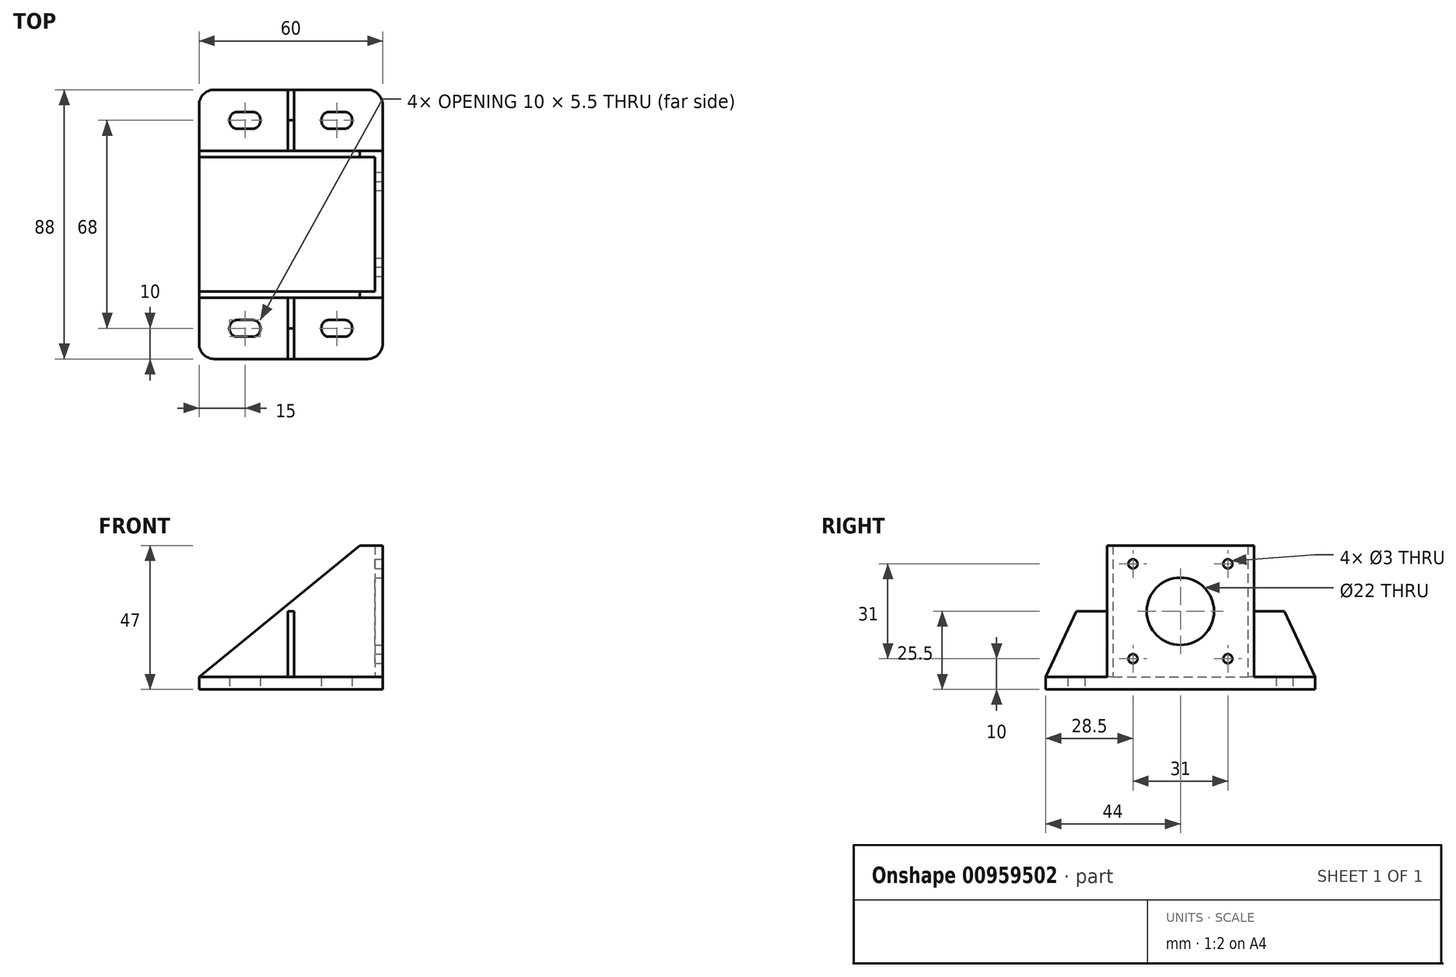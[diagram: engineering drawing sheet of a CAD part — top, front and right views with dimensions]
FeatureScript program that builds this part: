
annotation { "Feature Type Name" : "Feature", "Feature Type Description" : "" }
export const myFeature = defineFeature(function(context is Context, id is Id, definition is map)
    precondition{}
    {
        {
            var Q0;
            Q0=qCreatedBy(makeId("Top.planeOp"),FACE);
            var sketch = newSketch(context, id + "F0", { "sketchPlane" : qUnion([Q0])});
            skLineSegment(sketch, "E0.bottom", {"start": v(30, -24) * mm, "end": v(-30, -24) * mm});
            skLineSegment(sketch, "E0.top", {"start": v(30, 24) * mm, "end": v(-30, 24) * mm});
            skLineSegment(sketch, "E0.left", {"start": v(30, -24) * mm, "end": v(30, 24) * mm});
            skLineSegment(sketch, "E0.right", {"start": v(-30, -24) * mm, "end": v(-30, 24) * mm});
            skPoint(sketch, "E0.middle", {"position": v(0, 0) * mm});
            skLineSegment(sketch, "E1", {"start": v(-30, 22) * mm, "end": v(27.5, 22) * mm});
            skLineSegment(sketch, "E2", {"start": v(27.5, 22) * mm, "end": v(27.5, -22) * mm});
            skLineSegment(sketch, "E3", {"start": v(27.5, -22) * mm, "end": v(-30, -22) * mm});
            skLineSegment(sketch, "E4", {"start": v(30, -24) * mm, "end": v(30, -44) * mm});
            skLineSegment(sketch, "E5", {"start": v(30, -44) * mm, "end": v(-30, -44) * mm});
            skLineSegment(sketch, "E6", {"start": v(-30, -44) * mm, "end": v(-30, -24) * mm});
            skLineSegment(sketch, "E7", {"start": v(30, 24) * mm, "end": v(30, 44) * mm});
            skLineSegment(sketch, "E8", {"start": v(30, 44) * mm, "end": v(-30, 44) * mm});
            skLineSegment(sketch, "E9", {"start": v(-30, 44) * mm, "end": v(-30, 24) * mm});
            skLineSegment(sketch, "E10", {"start": v(-1, -44) * mm, "end": v(-1, -24) * mm});
            skLineSegment(sketch, "E11", {"start": v(1, -24) * mm, "end": v(1, -44) * mm});
            skLineSegment(sketch, "E12.MirrorCS", {"start": v(-1, 44) * mm, "end": v(-1, 24) * mm});
            skLineSegment(sketch, "E13.MirrorCS", {"start": v(1, 24) * mm, "end": v(1, 44) * mm});
            skLineSegment(sketch, "E14", {"start": v(30, -34) * mm, "end": v(-30, -34) * mm, "construction": true});
            skLineSegment(sketch, "E15.bottom", {"start": v(20, -36.75) * mm, "end": v(10, -36.75) * mm});
            skLineSegment(sketch, "E15.top", {"start": v(20, -31.25) * mm, "end": v(10, -31.25) * mm});
            skLineSegment(sketch, "E15.left", {"start": v(20, -36.75) * mm, "end": v(20, -31.25) * mm});
            skLineSegment(sketch, "E15.right", {"start": v(10, -36.75) * mm, "end": v(10, -31.25) * mm});
            skPoint(sketch, "E15.middle", {"position": v(15, -34) * mm});
            skLineSegment(sketch, "E16.bottom", {"start": v(-10, -36.75) * mm, "end": v(-20, -36.75) * mm});
            skLineSegment(sketch, "E16.top", {"start": v(-10, -31.25) * mm, "end": v(-20, -31.25) * mm});
            skLineSegment(sketch, "E16.left", {"start": v(-10, -36.75) * mm, "end": v(-10, -31.25) * mm});
            skLineSegment(sketch, "E16.right", {"start": v(-20, -36.75) * mm, "end": v(-20, -31.25) * mm});
            skPoint(sketch, "E16.middle", {"position": v(-15, -34) * mm});
            skLineSegment(sketch, "E17.MirrorCS", {"start": v(20, 31.25) * mm, "end": v(10, 31.25) * mm});
            skLineSegment(sketch, "E18.MirrorCS", {"start": v(20, 36.75) * mm, "end": v(20, 31.25) * mm});
            skLineSegment(sketch, "E19.MirrorCS", {"start": v(20, 36.75) * mm, "end": v(10, 36.75) * mm});
            skLineSegment(sketch, "E20.MirrorCS", {"start": v(10, 36.75) * mm, "end": v(10, 31.25) * mm});
            skLineSegment(sketch, "E21.MirrorCS", {"start": v(-10, 36.75) * mm, "end": v(-10, 31.25) * mm});
            skLineSegment(sketch, "E22.MirrorCS", {"start": v(-10, 36.75) * mm, "end": v(-20, 36.75) * mm});
            skLineSegment(sketch, "E23.MirrorCS", {"start": v(-20, 36.75) * mm, "end": v(-20, 31.25) * mm});
            skLineSegment(sketch, "E24.MirrorCS", {"start": v(-10, 31.25) * mm, "end": v(-20, 31.25) * mm});
            skSolve(sketch);
        }
        {
            var Q0;
            Q0 = qSketchRegion(id + "F0", true);
            extrude(context, id + "F1", {"entities" : qUnion([Q0]), "depth" : 4 * mm, "offsetDistance" : 25 * mm});
        }
        {
            var Q0;
            {var subQ1=sQuery(id+"F0.wireOp",EDGE,"E0.bottom");Q0=makeQuery(id+"F0.imprint","IMPRINT",FACE,{"disambiguationData":[TD([[makeQuery(id+"F0.imprint","IMPRINT",EDGE,{"derivedFrom":subQ1}),-1.0]])]});}
            var Q1;
            {var subQ0=sQuery(id+"F0.wireOp",EDGE,"E12.MirrorCS");Q1=makeQuery(id+"F0.imprint","IMPRINT",FACE,{"disambiguationData":[TD([[makeQuery(id+"F0.imprint","IMPRINT",EDGE,{"derivedFrom":subQ0}),1.0]])]});}
            var Q2;
            {var subQ0=sQuery(id+"F0.wireOp",EDGE,"E10");Q2=makeQuery(id+"F0.imprint","IMPRINT",FACE,{"disambiguationData":[TD([[makeQuery(id+"F0.imprint","IMPRINT",EDGE,{"derivedFrom":subQ0}),-1.0]])]});}
            extrude(context, id + "F2", {"entities" : qUnion([Q0, Q1, Q2]), "operationType" : NewBodyOperationType.ADD, "depth" : 47 * mm, "offsetDistance" : 25 * mm});
        }
        {
            var Q0;
            {var subQ0=sQuery(id+"F0.wireOp",EDGE,"E0.left");Q0=makeQuery(id+"F2.boolean.opBoolean","MERGE",FACE,{"derivedFrom":[makeQuery(id+"F1.opExtrude","SWEPT_FACE",FACE,{"disambiguationData":[OSD([subQ0,sQuery(id+"F0.wireOp",EDGE,"E4"),sQuery(id+"F0.wireOp",EDGE,"E7")])]}),makeQuery(id+"F2.opExtrude","SWEPT_FACE",FACE,{"disambiguationData":[OSD([subQ0])]})]});}
            var sketch = newSketch(context, id + "F3", { "sketchPlane" : qUnion([Q0])});
            skCircle(sketch, "E25", {"center": v(0, 25.5) * mm, "radius": 11 * mm});
            skLineSegment(sketch, "E26.bottom", {"start": v(15.5, 10) * mm, "end": v(-15.5, 10) * mm, "construction": true});
            skLineSegment(sketch, "E26.top", {"start": v(15.5, 41) * mm, "end": v(-15.5, 41) * mm, "construction": true});
            skLineSegment(sketch, "E26.left", {"start": v(15.5, 10) * mm, "end": v(15.5, 41) * mm, "construction": true});
            skLineSegment(sketch, "E26.right", {"start": v(-15.5, 10) * mm, "end": v(-15.5, 41) * mm, "construction": true});
            skCircle(sketch, "E27", {"center": v(-15.5, 41) * mm, "radius": 1.5 * mm});
            skCircle(sketch, "E28", {"center": v(15.5, 41) * mm, "radius": 1.5 * mm});
            skCircle(sketch, "E29", {"center": v(15.5, 10) * mm, "radius": 1.5 * mm});
            skCircle(sketch, "E30", {"center": v(-15.5, 10) * mm, "radius": 1.5 * mm});
            skSolve(sketch);
        }
        {
            var Q0;
            Q0 = qSketchRegion(id + "F3", true);
            extrude(context, id + "F4", {"entities" : qUnion([Q0]), "operationType" : NewBodyOperationType.REMOVE, "oppositeDirection" : true, "depth" : 25 * mm, "offsetDistance" : 25 * mm});
        }
        {
            var Q0;
            Q0=qCreatedBy(makeId("Right.planeOp"),FACE);
            var sketch = newSketch(context, id + "F5", { "sketchPlane" : qUnion([Q0])});
            skPoint(sketch, "E31.0", {"position": v(-44, 4) * mm});
            skPoint(sketch, "E32.0", {"position": v(-24, 47) * mm});
            skLineSegment(sketch, "E33", {"start": v(-44, 4) * mm, "end": v(-24, 47) * mm});
            skLineSegment(sketch, "E34", {"start": v(-44, 4) * mm, "end": v(-44, 47) * mm});
            skLineSegment(sketch, "E35", {"start": v(-44, 47) * mm, "end": v(-24, 47) * mm});
            skLineSegment(sketch, "E36.MirrorCS", {"start": v(44, 4) * mm, "end": v(24, 47) * mm});
            skLineSegment(sketch, "E37.MirrorCS", {"start": v(44, 47) * mm, "end": v(24, 47) * mm});
            skLineSegment(sketch, "E38.MirrorCS", {"start": v(44, 4) * mm, "end": v(44, 47) * mm});
            skLineSegment(sketch, "E39", {"start": v(-34, 25.5) * mm, "end": v(-24, 25.5) * mm});
            skLineSegment(sketch, "E40", {"start": v(-24, 25.5) * mm, "end": v(-24, 47) * mm});
            skLineSegment(sketch, "E41.MirrorCS", {"start": v(24, 25.5) * mm, "end": v(24, 47) * mm});
            skLineSegment(sketch, "E42.MirrorCS", {"start": v(34, 25.5) * mm, "end": v(24, 25.5) * mm});
            skSolve(sketch);
        }
        {
            var Q0;
            Q0 = qSketchRegion(id + "F5", true);
            extrude(context, id + "F6", {"entities" : qUnion([Q0]), "operationType" : NewBodyOperationType.REMOVE, "oppositeDirection" : true, "depth" : 25 * mm, "offsetDistance" : 25 * mm, "symmetric" : true});
        }
        {
            var Q0;
            Q0=qCreatedBy(makeId("Front.planeOp"),FACE);
            var sketch = newSketch(context, id + "F7", { "sketchPlane" : qUnion([Q0])});
            skPoint(sketch, "E43.0", {"position": v(-30, 4) * mm});
            skPoint(sketch, "E44.0", {"position": v(22.5, 47) * mm});
            skLineSegment(sketch, "E45", {"start": v(-30, 4) * mm, "end": v(22.5, 47) * mm});
            skLineSegment(sketch, "E46", {"start": v(22.5, 47) * mm, "end": v(-30, 47) * mm});
            skLineSegment(sketch, "E47", {"start": v(-30, 47) * mm, "end": v(-30, 4) * mm});
            skPoint(sketch, "E48.0", {"position": v(27.5, 47) * mm});
            skSolve(sketch);
        }
        {
            var Q0;
            Q0 = qSketchRegion(id + "F7", true);
            extrude(context, id + "F8", {"entities" : qUnion([Q0]), "operationType" : NewBodyOperationType.REMOVE, "oppositeDirection" : true, "depth" : 100 * mm, "offsetDistance" : 25 * mm, "symmetric" : true});
        }
        {
            var Q0;
            Q0=makeQuery(id+"F1.opExtrude","SWEPT_EDGE",EDGE,{"disambiguationData":[OSD([sQuery(id+"F0.wireOp",EDGE,"E22.MirrorCS"),sQuery(id+"F0.wireOp",EDGE,"E23.MirrorCS")])]});
            var Q1;
            Q1=makeQuery(id+"F1.opExtrude","SWEPT_EDGE",EDGE,{"disambiguationData":[OSD([sQuery(id+"F0.wireOp",EDGE,"E23.MirrorCS"),sQuery(id+"F0.wireOp",EDGE,"E24.MirrorCS")])]});
            var Q2;
            Q2=makeQuery(id+"F1.opExtrude","SWEPT_EDGE",EDGE,{"disambiguationData":[OSD([sQuery(id+"F0.wireOp",EDGE,"E21.MirrorCS"),sQuery(id+"F0.wireOp",EDGE,"E22.MirrorCS")])]});
            var Q3;
            Q3=makeQuery(id+"F1.opExtrude","SWEPT_EDGE",EDGE,{"disambiguationData":[OSD([sQuery(id+"F0.wireOp",EDGE,"E21.MirrorCS"),sQuery(id+"F0.wireOp",EDGE,"E24.MirrorCS")])]});
            var Q4;
            Q4=makeQuery(id+"F1.opExtrude","SWEPT_EDGE",EDGE,{"disambiguationData":[OSD([sQuery(id+"F0.wireOp",EDGE,"E17.MirrorCS"),sQuery(id+"F0.wireOp",EDGE,"E18.MirrorCS")])]});
            var Q5;
            Q5=makeQuery(id+"F1.opExtrude","SWEPT_EDGE",EDGE,{"disambiguationData":[OSD([sQuery(id+"F0.wireOp",EDGE,"E15.bottom"),sQuery(id+"F0.wireOp",EDGE,"E15.left")])]});
            var Q6;
            Q6=makeQuery(id+"F1.opExtrude","SWEPT_EDGE",EDGE,{"disambiguationData":[OSD([sQuery(id+"F0.wireOp",EDGE,"E16.bottom"),sQuery(id+"F0.wireOp",EDGE,"E16.left")])]});
            var Q7;
            Q7=makeQuery(id+"F1.opExtrude","SWEPT_EDGE",EDGE,{"disambiguationData":[OSD([sQuery(id+"F0.wireOp",EDGE,"E15.top"),sQuery(id+"F0.wireOp",EDGE,"E15.left")])]});
            var Q8;
            Q8=makeQuery(id+"F1.opExtrude","SWEPT_EDGE",EDGE,{"disambiguationData":[OSD([sQuery(id+"F0.wireOp",EDGE,"E16.top"),sQuery(id+"F0.wireOp",EDGE,"E16.left")])]});
            var Q9;
            Q9=makeQuery(id+"F1.opExtrude","SWEPT_EDGE",EDGE,{"disambiguationData":[OSD([sQuery(id+"F0.wireOp",EDGE,"E18.MirrorCS"),sQuery(id+"F0.wireOp",EDGE,"E19.MirrorCS")])]});
            var Q10;
            Q10=makeQuery(id+"F1.opExtrude","SWEPT_EDGE",EDGE,{"disambiguationData":[OSD([sQuery(id+"F0.wireOp",EDGE,"E16.bottom"),sQuery(id+"F0.wireOp",EDGE,"E16.right")])]});
            var Q11;
            Q11=makeQuery(id+"F1.opExtrude","SWEPT_EDGE",EDGE,{"disambiguationData":[OSD([sQuery(id+"F0.wireOp",EDGE,"E15.bottom"),sQuery(id+"F0.wireOp",EDGE,"E15.right")])]});
            var Q12;
            Q12=makeQuery(id+"F1.opExtrude","SWEPT_EDGE",EDGE,{"disambiguationData":[OSD([sQuery(id+"F0.wireOp",EDGE,"E17.MirrorCS"),sQuery(id+"F0.wireOp",EDGE,"E20.MirrorCS")])]});
            var Q13;
            Q13=makeQuery(id+"F1.opExtrude","SWEPT_EDGE",EDGE,{"disambiguationData":[OSD([sQuery(id+"F0.wireOp",EDGE,"E16.top"),sQuery(id+"F0.wireOp",EDGE,"E16.right")])]});
            var Q14;
            Q14=makeQuery(id+"F1.opExtrude","SWEPT_EDGE",EDGE,{"disambiguationData":[OSD([sQuery(id+"F0.wireOp",EDGE,"E15.top"),sQuery(id+"F0.wireOp",EDGE,"E15.right")])]});
            var Q15;
            Q15=makeQuery(id+"F1.opExtrude","SWEPT_EDGE",EDGE,{"disambiguationData":[OSD([sQuery(id+"F0.wireOp",EDGE,"E19.MirrorCS"),sQuery(id+"F0.wireOp",EDGE,"E20.MirrorCS")])]});
            fillet(context, id + "F9", {"entities" : qUnion([Q0, Q1, Q2, Q3, Q4, Q5, Q6, Q7, Q8, Q9, Q10, Q11, Q12, Q13, Q14, Q15]), "radius" : 2.5 * mm, "tangentPropagation" : true, "allowEdgeOverflow" : false});
        }
        {
            var Q0;
            Q0=makeQuery(id+"F1.opExtrude","SWEPT_EDGE",EDGE,{"disambiguationData":[OSD([sQuery(id+"F0.wireOp",EDGE,"E5"),sQuery(id+"F0.wireOp",EDGE,"E6")])]});
            var Q1;
            Q1=makeQuery(id+"F1.opExtrude","SWEPT_EDGE",EDGE,{"disambiguationData":[OSD([sQuery(id+"F0.wireOp",EDGE,"E4"),sQuery(id+"F0.wireOp",EDGE,"E5")])]});
            var Q2;
            Q2=makeQuery(id+"F1.opExtrude","SWEPT_EDGE",EDGE,{"disambiguationData":[OSD([sQuery(id+"F0.wireOp",EDGE,"E7"),sQuery(id+"F0.wireOp",EDGE,"E8")])]});
            var Q3;
            Q3=makeQuery(id+"F1.opExtrude","SWEPT_EDGE",EDGE,{"disambiguationData":[OSD([sQuery(id+"F0.wireOp",EDGE,"E8"),sQuery(id+"F0.wireOp",EDGE,"E9")])]});
            fillet(context, id + "F10", {"entities" : qUnion([Q0, Q1, Q2, Q3]), "radius" : 5 * mm, "tangentPropagation" : true, "allowEdgeOverflow" : false});
        }
    });
